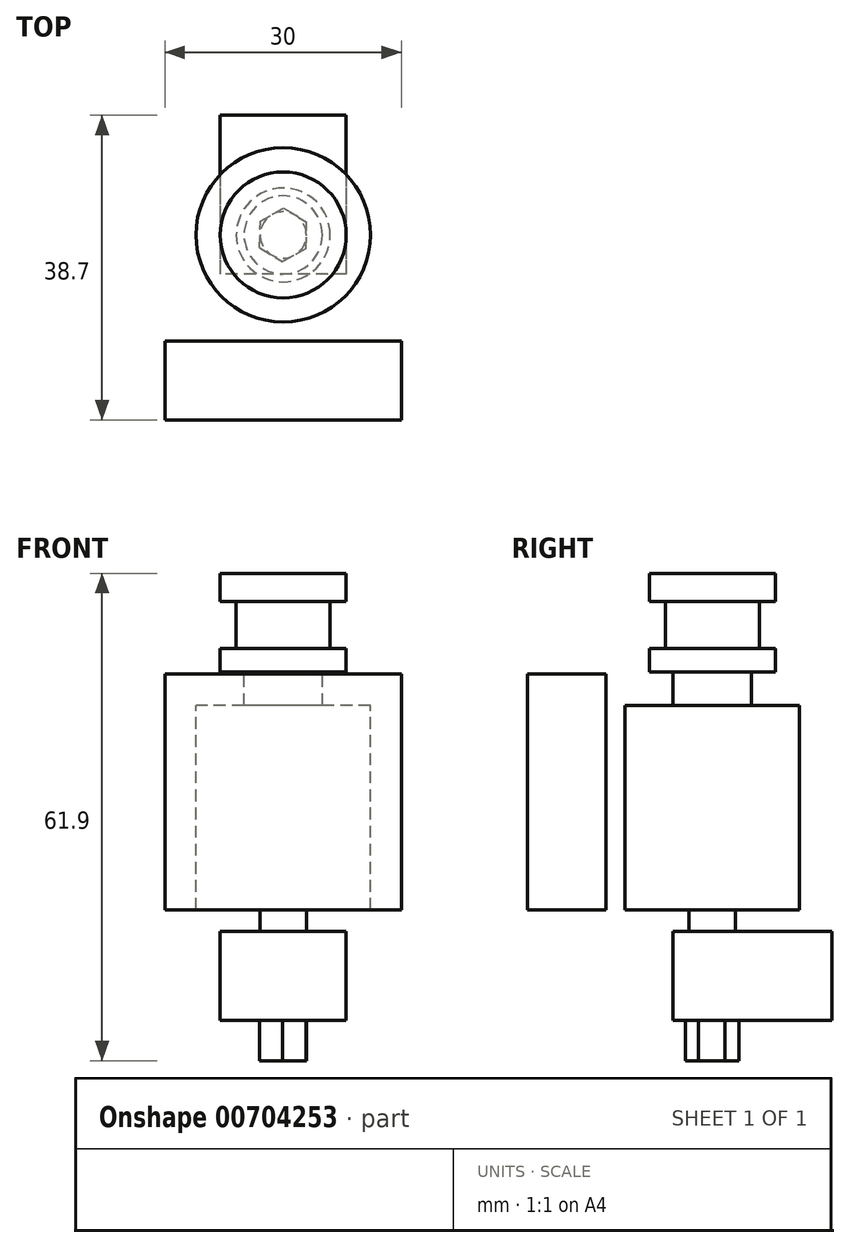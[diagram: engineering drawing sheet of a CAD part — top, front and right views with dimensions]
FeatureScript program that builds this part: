
annotation { "Feature Type Name" : "Feature", "Feature Type Description" : "" }
export const myFeature = defineFeature(function(context is Context, id is Id, definition is map)
    precondition{}
    {
        {
            var Q0;
            Q0=qCreatedBy(makeId("Front.planeOp"),FACE);
            var sketch = newSketch(context, id + "F0", { "sketchPlane" : qUnion([Q0])});
            skLineSegment(sketch, "E0", {"start": v(0, 42.75) * mm, "end": v(8, 42.75) * mm});
            skLineSegment(sketch, "E1", {"start": v(8, 42.75) * mm, "end": v(8, 39.2) * mm});
            skLineSegment(sketch, "E2", {"start": v(8, 39.2) * mm, "end": v(5.96, 39.2) * mm});
            skLineSegment(sketch, "E3", {"start": v(5.96, 39.2) * mm, "end": v(5.96, 33.2) * mm});
            skLineSegment(sketch, "E4", {"start": v(5.96, 33.2) * mm, "end": v(8, 33.2) * mm});
            skLineSegment(sketch, "E5", {"start": v(8, 33.2) * mm, "end": v(8, 30.2) * mm});
            skLineSegment(sketch, "E6", {"start": v(8, 30.2) * mm, "end": v(4.97, 30.2) * mm});
            skLineSegment(sketch, "E7", {"start": v(4.97, 30.2) * mm, "end": v(4.97, 26) * mm});
            skLineSegment(sketch, "E8", {"start": v(4.97, 26) * mm, "end": v(11.07, 26) * mm});
            skLineSegment(sketch, "E9", {"start": v(11.07, 26) * mm, "end": v(11.07, 0) * mm});
            skLineSegment(sketch, "E10", {"start": v(11.07, 0) * mm, "end": v(0, 0) * mm});
            skLineSegment(sketch, "E11", {"start": v(0, 42.75) * mm, "end": v(0, 0) * mm});
            skSolve(sketch);
        }
        {
            var Q0;
            Q0 = qSketchRegion(id + "F0", true);
            var Q1;
            Q1=sQuery(id+"F0.wireOp",EDGE,"E11");
            revolve(context, id + "F1", {"surfaceOperationType" : NewSurfaceOperationType.NEW, "entities" : qUnion([Q0]), "axis" : qUnion([Q1]), "revolveType" : RevolveType.FULL});
        }
        {
            var Q0;
            Q0=makeQuery(id+"F1.opRevolve","SWEPT_FACE",FACE,{"disambiguationData":[OSD([sQuery(id+"F0.wireOp",EDGE,"E10")])]});
            var sketch = newSketch(context, id + "F2", { "sketchPlane" : qUnion([Q0])});
            skCircle(sketch, "E12", {"center": v(0, 0) * mm, "radius": 2.94 * mm});
            skSolve(sketch);
        }
        {
            var Q0;
            Q0 = qSketchRegion(id + "F2", true);
            extrude(context, id + "F3", {"entities" : qUnion([Q0]), "operationType" : NewBodyOperationType.ADD, "depth" : 7.65 * mm, "offsetDistance" : 25 * mm});
        }
        {
            var Q0;
            Q0=qCreatedBy(makeId("Front.planeOp"),FACE);
            cPlane(context, id + "F4", {"entities" : qUnion([Q0]), "cplaneType" : CPlaneType.OFFSET, "offset" : (36.5 - 13) * mm, "width" : 150 * mm, "height" : 150 * mm});
        }
        {
            var Q0;
            Q0=qCreatedBy(id+"F4.planeOp",FACE);
            var sketch = newSketch(context, id + "F5", { "sketchPlane" : qUnion([Q0])});
            skLineSegment(sketch, "E13", {"start": v(0, 53.98) * mm, "end": v(0, -30.34) * mm, "construction": true});
            skLineSegment(sketch, "E14.bottom", {"start": v(-15, 30) * mm, "end": v(15, 30) * mm});
            skLineSegment(sketch, "E14.top", {"start": v(-15, 0) * mm, "end": v(15, 0) * mm});
            skLineSegment(sketch, "E14.left", {"start": v(-15, 30) * mm, "end": v(-15, 0) * mm});
            skLineSegment(sketch, "E14.right", {"start": v(15, 30) * mm, "end": v(15, 0) * mm});
            skSolve(sketch);
        }
        {
            var Q0;
            Q0 = qSketchRegion(id + "F5", true);
            extrude(context, id + "F6", {"entities" : qUnion([Q0]), "depth" : -10 * mm, "offsetDistance" : 25 * mm});
        }
        {
            var Q0;
            Q0=qCreatedBy(makeId("Right.planeOp"),FACE);
            var sketch = newSketch(context, id + "F7", { "sketchPlane" : qUnion([Q0])});
            skLineSegment(sketch, "E15.bottom", {"start": v(15.2, -2.7) * mm, "end": v(-5, -2.7) * mm});
            skLineSegment(sketch, "E15.top", {"start": v(15.2, -14) * mm, "end": v(-5, -14) * mm});
            skLineSegment(sketch, "E15.left", {"start": v(15.2, -2.7) * mm, "end": v(15.2, -14) * mm});
            skLineSegment(sketch, "E15.right", {"start": v(-5, -2.7) * mm, "end": v(-5, -14) * mm});
            skSolve(sketch);
        }
        {
            var Q0;
            Q0=makeQuery(id+"F7.imprint","IMPRINT",FACE,{"disambiguationData":[TD([[makeQuery(id+"F7.imprint","IMPRINT",EDGE,{"derivedFrom":sQuery(id+"F7.wireOp",EDGE,"E15.bottom")}),1.0]])]});
            extrude(context, id + "F8", {"entities" : qUnion([Q0]), "operationType" : NewBodyOperationType.ADD, "depth" : 16 * mm, "offsetDistance" : 25 * mm, "symmetric" : true});
        }
        {
            var Q0;
            Q0=makeQuery(id+"F8.opExtrude","SWEPT_FACE",FACE,{"disambiguationData":[OSD([sQuery(id+"F7.wireOp",EDGE,"E15.top")])]});
            var sketch = newSketch(context, id + "F9", { "sketchPlane" : qUnion([Q0])});
            skCircle(sketch, "E16.0", {"center": v(0, 0) * mm, "radius": 2.94 * mm, "construction": true});
            skLineSegment(sketch, "E17.0", {"start": v(-0.07, 3.4) * mm, "end": v(2.9, 1.76) * mm, "construction": true});
            skLineSegment(sketch, "E17.1", {"start": v(2.9, 1.76) * mm, "end": v(2.98, -1.63) * mm, "construction": true});
            skLineSegment(sketch, "E17.2", {"start": v(2.98, -1.63) * mm, "end": v(0.07, -3.4) * mm, "construction": true});
            skLineSegment(sketch, "E17.3", {"start": v(0.07, -3.4) * mm, "end": v(-2.9, -1.76) * mm, "construction": true});
            skLineSegment(sketch, "E17.4", {"start": v(-2.9, -1.76) * mm, "end": v(-2.98, 1.63) * mm, "construction": true});
            skLineSegment(sketch, "E17.5", {"start": v(-2.98, 1.63) * mm, "end": v(-0.07, 3.4) * mm, "construction": true});
            skPoint(sketch, "E17.0.midPoint", {"position": v(1.42, 2.58) * mm});
            skLineSegment(sketch, "E18", {"start": v(0.07, -3.4) * mm, "end": v(2.98, -1.63) * mm});
            skLineSegment(sketch, "E19", {"start": v(2.9, 1.76) * mm, "end": v(-0.07, 3.4) * mm});
            skLineSegment(sketch, "E20", {"start": v(-2.98, 1.63) * mm, "end": v(-2.9, -1.76) * mm});
            skLineSegment(sketch, "E21", {"start": v(-2.9, -1.76) * mm, "end": v(0.07, -3.4) * mm});
            skLineSegment(sketch, "E22", {"start": v(-2.98, 1.63) * mm, "end": v(-0.07, 3.4) * mm});
            skLineSegment(sketch, "E23", {"start": v(2.9, 1.76) * mm, "end": v(2.98, -1.63) * mm});
            skSolve(sketch);
        }
        {
            var Q0;
            Q0 = qSketchRegion(id + "F9", true);
            extrude(context, id + "F10", {"entities" : qUnion([Q0]), "operationType" : NewBodyOperationType.ADD, "depth" : 5.15 * mm, "offsetDistance" : 25 * mm});
        }
    });
